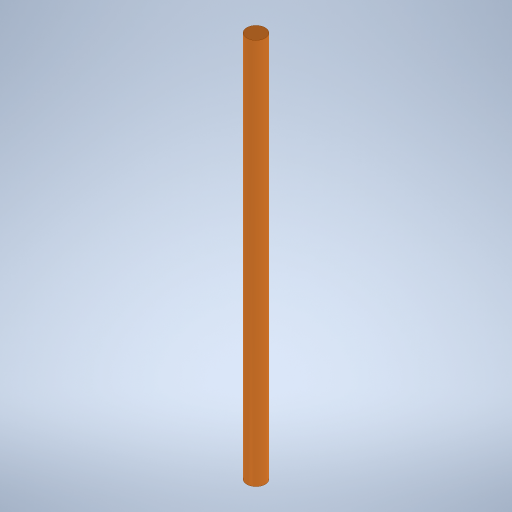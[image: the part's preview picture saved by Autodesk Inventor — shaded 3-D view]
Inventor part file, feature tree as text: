
AUTODESK INVENTOR PART (.ipt)
format: ipt  version: 2023 (Build 270158000, 158)  size: 260,608 bytes
history: native  units: in
note: dims shown in document units (in); Inventor stores cm internally (conversion verified against a paired STEP export)
features: sketch x9, extrude x8, fillet x2
ambient origin geometry x8: Origin, YZ Plane, XZ Plane, XY Plane, X Axis, Y Axis, Z Axis, Center Point
bodies: Solid1 (feature_tree)
feature tree (19):
  sketch  "Sketch1"  dims[d0=0.2362in d1=4.5669in d2=0.0in]
  extrude  "Extrusion1"  Depth=4.5669in TaperAngle=0.0deg
  extrude  "Extrusion2"  Depth=0.3937in
  extrude  "Extrusion3"  Depth=0.3937in
  fillet  "Fillet1"  Radius=0.0787in
  fillet  "Face Fillet1"
  extrude  "Extrusion4"  Depth=0.0394in TaperAngle=0.0deg
  extrude  "Extrusion5"  Depth=0.1181in TaperAngle=0.0deg
  extrude  "Extrusion6"  Depth=0.0787in TaperAngle=0.0deg
  extrude  "Extrusion7"  Depth=0.0394in TaperAngle=0.0deg
  extrude  "Extrusion8"  [1 undecoded]
  sketch  "Sketch2"  dims[d3=0.3937in d4=0.0in d5=0.2362in]
  sketch  "Sketch3"  dims[d6=0.3937in d7=0.0in d8=0.0787in d9=0.0787in]
  sketch  "Sketch4"  dims[d10=0.0787in d11=0.0in d12=0.0394in d13=0.0in]
  sketch  "Sketch5"  dims[d14=0.2362in d15=0.1181in d16=0.0in]
  sketch  "Sketch6"  dims[d17=0.2362in d18=0.0787in d19=0.0in]
  sketch  "Sketch7"  dims[d20=0.2362in d21=0.0394in d22=0.0in]
  sketch  "Sketch8"
  sketch  "Sketch9"
note: 1 required parameter value undecoded (feature->parameter linkage not recoverable at this tier; creation-order binding heuristic only, values carry confidence <= 0.55)
